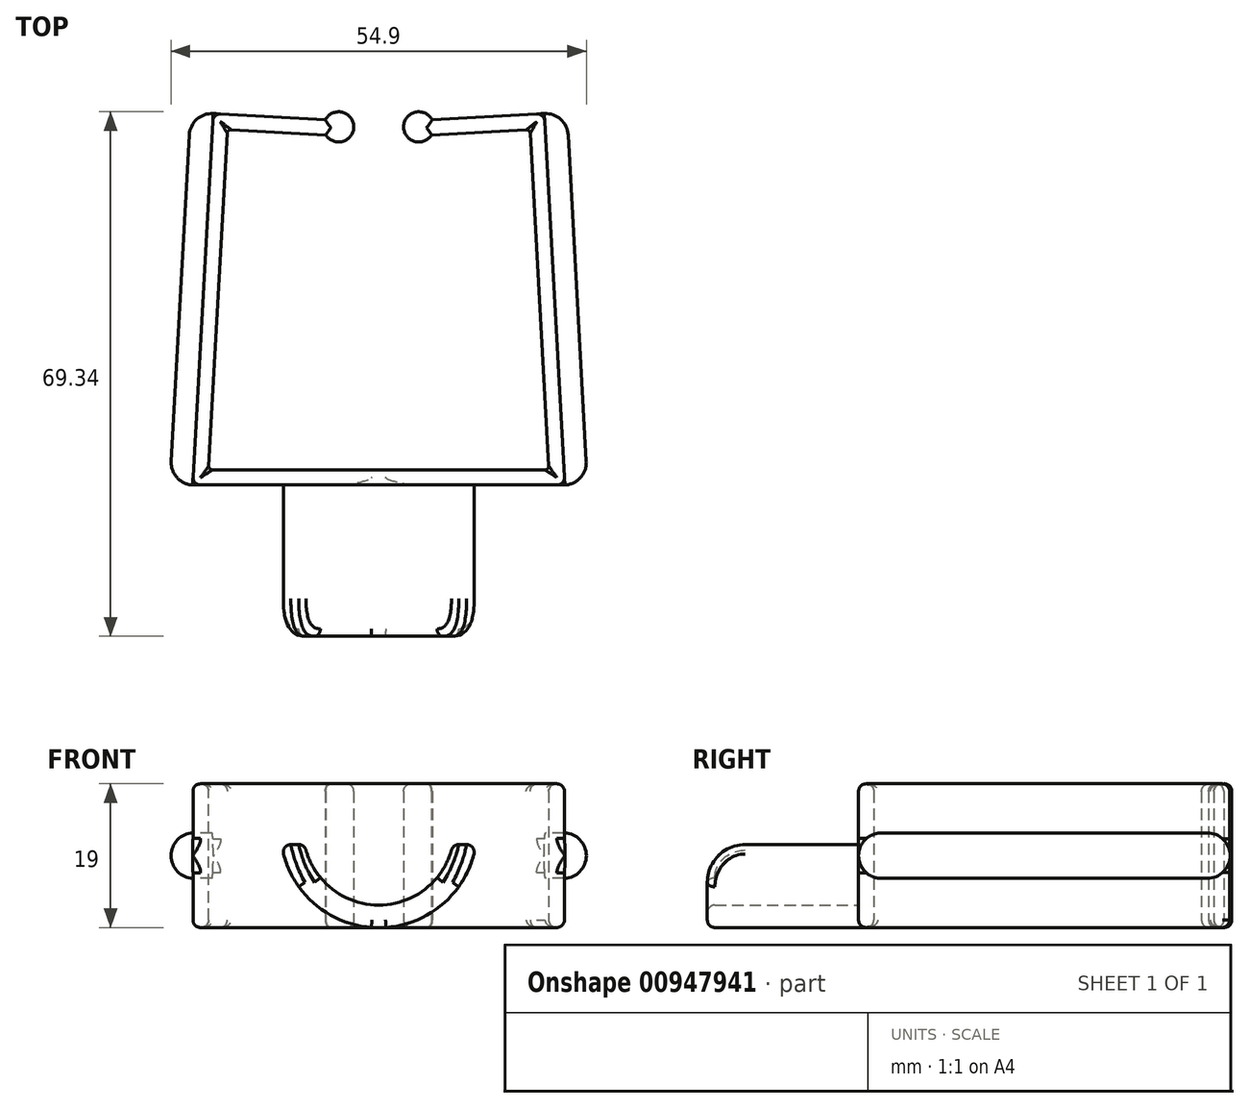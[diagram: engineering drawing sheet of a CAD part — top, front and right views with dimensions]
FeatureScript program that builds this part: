
annotation { "Feature Type Name" : "Feature", "Feature Type Description" : "" }
export const myFeature = defineFeature(function(context is Context, id is Id, definition is map)
    precondition{}
    {
        {
            var Q0;
            Q0=qCreatedBy(makeId("Top.planeOp"),FACE);
            var sketch = newSketch(context, id + "F0", { "sketchPlane" : qUnion([Q0])});
            skLineSegment(sketch, "E0", {"start": v(0, -31.5) * mm, "end": v(22.5, -31.5) * mm});
            skLineSegment(sketch, "E1", {"start": v(20, 13.5) * mm, "end": v(22.5, -31.5) * mm});
            skLineSegment(sketch, "E2", {"start": v(20, 13.5) * mm, "end": v(7, 12.78) * mm});
            skLineSegment(sketch, "E3.0", {"start": v(0, -33.5) * mm, "end": v(24.62, -33.5) * mm});
            skLineSegment(sketch, "E4.0", {"start": v(21.89, 15.61) * mm, "end": v(24.62, -33.5) * mm});
            skLineSegment(sketch, "E5.0", {"start": v(21.89, 15.61) * mm, "end": v(7.06, 14.8) * mm});
            skLineSegment(sketch, "E6.MirrorCS", {"start": v(-21.88, 15.61) * mm, "end": v(-24.61, -33.5) * mm});
            skLineSegment(sketch, "E7.MirrorCS", {"start": v(-20, 13.5) * mm, "end": v(-22.5, -31.5) * mm});
            skLineSegment(sketch, "E8.MirrorCS", {"start": v(0, -31.5) * mm, "end": v(-22.5, -31.5) * mm});
            skLineSegment(sketch, "E9.MirrorCS", {"start": v(0, -33.5) * mm, "end": v(-24.61, -33.5) * mm});
            skArc(sketch, "E10", {"start": v(7.06, 14.8) * mm, "mid": v(3.3, 13.92) * mm, "end": v(7, 12.78) * mm});
            skLineSegment(sketch, "E11.MirrorCS", {"start": v(-21.89, 15.61) * mm, "end": v(-7.06, 14.8) * mm});
            skLineSegment(sketch, "E12.MirrorCS", {"start": v(-20, 13.5) * mm, "end": v(-7, 12.78) * mm});
            skArc(sketch, "E13.MirrorCS", {"start": v(-7.06, 14.8) * mm, "mid": v(-3.3, 13.92) * mm, "end": v(-7, 12.78) * mm});
            skSolve(sketch);
        }
        {
            var Q0;
            Q0=makeQuery(id+"F0.imprint","IMPRINT",FACE,{"disambiguationData":[TD([[makeQuery(id+"F0.imprint","IMPRINT",EDGE,{"derivedFrom":sQuery(id+"F0.wireOp",EDGE,"E0")}),-1.0]])]});
            extrude(context, id + "F1", {"entities" : qUnion([Q0]), "depth" : 19 * mm, "offsetDistance" : 25 * mm});
        }
        {
            var Q0;
            Q0=makeQuery(id+"F1.opExtrude","SWEPT_FACE",FACE,{"disambiguationData":[OSD([sQuery(id+"F0.wireOp",EDGE,"E6.MirrorCS")])]});
            var sketch = newSketch(context, id + "F2", { "sketchPlane" : qUnion([Q0])});
            skLineSegment(sketch, "E14", {"start": v(-14.38, 12.5) * mm, "end": v(34.8, 12.5) * mm});
            skLineSegment(sketch, "E15", {"start": v(-14.38, 6.5) * mm, "end": v(34.8, 6.5) * mm});
            skLineSegment(sketch, "E16", {"start": v(-14.38, 12.5) * mm, "end": v(-14.38, 6.5) * mm});
            skLineSegment(sketch, "E17", {"start": v(34.8, 12.5) * mm, "end": v(34.8, 6.5) * mm});
            skSolve(sketch);
        }
        {
            var Q0;
            Q0=makeQuery(id+"F2.imprint","IMPRINT",FACE,{"disambiguationData":[TD([[makeQuery(id+"F2.imprint","IMPRINT",EDGE,{"derivedFrom":sQuery(id+"F2.wireOp",EDGE,"E14")}),-1.0]])]});
            extrude(context, id + "F3", {"entities" : qUnion([Q0]), "operationType" : NewBodyOperationType.ADD, "depth" : 3 * mm, "offsetDistance" : 25 * mm});
        }
        {
            var Q0;
            Q0=makeQuery(id+"F1.opExtrude","SWEPT_FACE",FACE,{"disambiguationData":[OSD([sQuery(id+"F0.wireOp",EDGE,"E4.0")])]});
            var sketch = newSketch(context, id + "F4", { "sketchPlane" : qUnion([Q0])});
            skLineSegment(sketch, "E18", {"start": v(-34.8, 12.5) * mm, "end": v(14.38, 12.5) * mm});
            skLineSegment(sketch, "E19", {"start": v(-34.8, 6.5) * mm, "end": v(14.38, 6.5) * mm});
            skLineSegment(sketch, "E20", {"start": v(-34.8, 12.5) * mm, "end": v(-34.8, 6.5) * mm});
            skLineSegment(sketch, "E21", {"start": v(14.38, 12.5) * mm, "end": v(14.38, 6.5) * mm});
            skSolve(sketch);
        }
        {
            var Q0;
            Q0=makeQuery(id+"F4.imprint","IMPRINT",FACE,{"disambiguationData":[TD([[makeQuery(id+"F4.imprint","IMPRINT",EDGE,{"derivedFrom":sQuery(id+"F4.wireOp",EDGE,"E18")}),-1.0]])]});
            extrude(context, id + "F5", {"entities" : qUnion([Q0]), "operationType" : NewBodyOperationType.ADD, "depth" : 3 * mm, "offsetDistance" : 25 * mm});
        }
        {
            var Q0;
            Q0=makeQuery(id+"F5.opExtrude","CAP_EDGE",EDGE,{"disambiguationData":[OSD([sQuery(id+"F4.wireOp",EDGE,"E18")])],"isStart":false});
            var Q1;
            Q1=makeQuery(id+"F5.opExtrude","CAP_EDGE",EDGE,{"disambiguationData":[OSD([sQuery(id+"F4.wireOp",EDGE,"E19")])],"isStart":false});
            var Q2;
            Q2=makeQuery(id+"F5.opExtrude","CAP_EDGE",EDGE,{"disambiguationData":[OSD([sQuery(id+"F4.wireOp",EDGE,"E20")])],"isStart":false});
            var Q3;
            Q3=makeQuery(id+"F5.opExtrude","SWEPT_EDGE",EDGE,{"disambiguationData":[OSD([sQuery(id+"F0.wireOp",EDGE,"E3.0"),sQuery(id+"F0.wireOp",EDGE,"E4.0"),sQuery(id+"F4.wireOp",EDGE,"E18"),sQuery(id+"F4.wireOp",EDGE,"E20")])]});
            var Q4;
            Q4=makeQuery(id+"F5.opExtrude","SWEPT_EDGE",EDGE,{"disambiguationData":[OSD([sQuery(id+"F0.wireOp",EDGE,"E3.0"),sQuery(id+"F0.wireOp",EDGE,"E4.0"),sQuery(id+"F4.wireOp",EDGE,"E19"),sQuery(id+"F4.wireOp",EDGE,"E20")])]});
            var Q5;
            Q5=makeQuery(id+"F5.opExtrude","CAP_EDGE",EDGE,{"disambiguationData":[OSD([sQuery(id+"F4.wireOp",EDGE,"E21")])],"isStart":false});
            var Q6;
            Q6=makeQuery(id+"F5.opExtrude","SWEPT_EDGE",EDGE,{"disambiguationData":[OSD([sQuery(id+"F0.wireOp",EDGE,"E4.0"),sQuery(id+"F0.wireOp",EDGE,"E5.0"),sQuery(id+"F4.wireOp",EDGE,"E18"),sQuery(id+"F4.wireOp",EDGE,"E21")])]});
            var Q7;
            Q7=makeQuery(id+"F5.opExtrude","SWEPT_EDGE",EDGE,{"disambiguationData":[OSD([sQuery(id+"F0.wireOp",EDGE,"E4.0"),sQuery(id+"F0.wireOp",EDGE,"E5.0"),sQuery(id+"F4.wireOp",EDGE,"E19"),sQuery(id+"F4.wireOp",EDGE,"E21")])]});
            var Q8;
            Q8=makeQuery(id+"F3.opExtrude","CAP_EDGE",EDGE,{"disambiguationData":[OSD([sQuery(id+"F2.wireOp",EDGE,"E14")])],"isStart":false});
            var Q9;
            Q9=makeQuery(id+"F3.opExtrude","CAP_EDGE",EDGE,{"disambiguationData":[OSD([sQuery(id+"F2.wireOp",EDGE,"E15")])],"isStart":false});
            var Q10;
            Q10=makeQuery(id+"F3.opExtrude","CAP_EDGE",EDGE,{"disambiguationData":[OSD([sQuery(id+"F2.wireOp",EDGE,"E16")])],"isStart":false});
            var Q11;
            Q11=makeQuery(id+"F3.opExtrude","SWEPT_EDGE",EDGE,{"disambiguationData":[OSD([sQuery(id+"F0.wireOp",EDGE,"571edef0-3b51-43ca-9341-9ceadd8f7e81.MirrorCS"),sQuery(id+"F0.wireOp",EDGE,"E6.MirrorCS"),sQuery(id+"F2.wireOp",EDGE,"E15"),sQuery(id+"F2.wireOp",EDGE,"E16")])]});
            var Q12;
            Q12=makeQuery(id+"F3.opExtrude","SWEPT_EDGE",EDGE,{"disambiguationData":[OSD([sQuery(id+"F0.wireOp",EDGE,"571edef0-3b51-43ca-9341-9ceadd8f7e81.MirrorCS"),sQuery(id+"F0.wireOp",EDGE,"E6.MirrorCS"),sQuery(id+"F2.wireOp",EDGE,"E14"),sQuery(id+"F2.wireOp",EDGE,"E16")])]});
            var Q13;
            Q13=makeQuery(id+"F3.opExtrude","CAP_EDGE",EDGE,{"disambiguationData":[OSD([sQuery(id+"F2.wireOp",EDGE,"E17")])],"isStart":false});
            var Q14;
            Q14=makeQuery(id+"F3.opExtrude","SWEPT_EDGE",EDGE,{"disambiguationData":[OSD([sQuery(id+"F0.wireOp",EDGE,"E6.MirrorCS"),sQuery(id+"F0.wireOp",EDGE,"E9.MirrorCS"),sQuery(id+"F2.wireOp",EDGE,"E14"),sQuery(id+"F2.wireOp",EDGE,"E17")])]});
            var Q15;
            Q15=makeQuery(id+"F3.opExtrude","SWEPT_EDGE",EDGE,{"disambiguationData":[OSD([sQuery(id+"F0.wireOp",EDGE,"E6.MirrorCS"),sQuery(id+"F0.wireOp",EDGE,"E9.MirrorCS"),sQuery(id+"F2.wireOp",EDGE,"E15"),sQuery(id+"F2.wireOp",EDGE,"E17")])]});
            fillet(context, id + "F6", {"entities" : qUnion([Q0, Q1, Q2, Q3, Q4, Q5, Q6, Q7, Q8, Q9, Q10, Q11, Q12, Q13, Q14, Q15]), "radius" : 3 * mm, "tangentPropagation" : true, "allowEdgeOverflow" : false});
        }
        {
            var Q0;
            Q0=makeQuery(id+"F1.opExtrude","SWEPT_FACE",FACE,{"disambiguationData":[OSD([sQuery(id+"F0.wireOp",EDGE,"E3.0"),sQuery(id+"F0.wireOp",EDGE,"E9.MirrorCS")])]});
            var sketch = newSketch(context, id + "F7", { "sketchPlane" : qUnion([Q0])});
            skArc(sketch, "E22", {"start": v(-9.8, 10.97) * mm, "mid": v(0, 2.97) * mm, "end": v(9.8, 10.97) * mm});
            skLineSegment(sketch, "E23", {"start": v(-9.8, 10.97) * mm, "end": v(-12.82, 10.97) * mm});
            skLineSegment(sketch, "E24", {"start": v(9.8, 10.97) * mm, "end": v(12.85, 10.97) * mm});
            skArc(sketch, "E25", {"start": v(-12.85, 10.97) * mm, "mid": v(0, -0.03) * mm, "end": v(12.85, 10.97) * mm});
            skLineSegment(sketch, "E26", {"start": v(-12.82, 10.97) * mm, "end": v(-12.85, 10.97) * mm});
            skPoint(sketch, "E27.start.orphan", {"position": v(0, 0) * mm});
            skSolve(sketch);
        }
        {
            var Q0;
            Q0=makeQuery(id+"F7.imprint","IMPRINT",FACE,{"disambiguationData":[TD([[makeQuery(id+"F7.imprint","IMPRINT",EDGE,{"derivedFrom":sQuery(id+"F7.wireOp",EDGE,"E22")}),-1.0]])]});
            extrude(context, id + "F8", {"entities" : qUnion([Q0]), "operationType" : NewBodyOperationType.ADD, "depth" : 20 * mm, "offsetDistance" : 25 * mm});
        }
        {
            var Q0;
            Q0=makeQuery(id+"F8.opExtrude","CAP_EDGE",EDGE,{"disambiguationData":[OSD([sQuery(id+"F7.wireOp",EDGE,"E27"),sQuery(id+"F7.wireOp",EDGE,"a4f32ab0-1648-429d-a977-f9504d9d67a10.MirrorCS")])],"isStart":false});
            var Q1;
            Q1=makeQuery(id+"F8.opExtrude","SWEPT_EDGE",EDGE,{"disambiguationData":[OSD([sQuery(id+"F7.wireOp",EDGE,"a4f32ab0-1648-429d-a977-f9504d9d67a10.MirrorCS"),sQuery(id+"F7.wireOp",EDGE,"80b11956-c133-4d79-b513-8fb03a3275040.MirrorCS")])]});
            var Q2;
            Q2=makeQuery(id+"F8.opExtrude","SWEPT_EDGE",EDGE,{"disambiguationData":[OSD([sQuery(id+"F7.wireOp",EDGE,"EQUY75fL-QU1j-GgtN-3R5t-ZK2hIXwrbhZ0"),sQuery(id+"F7.wireOp",EDGE,"E27")])]});
            var Q3;
            {var subQ0=sQuery(id+"F7.wireOp",EDGE,"E25");Q3=makeQuery(id+"F8.opExtrude","CAP_EDGE",EDGE,{"disambiguationData":[OSD([subQ0]),TDD([makeQuery(id+"F7.imprint","IMPRINT",EDGE,{"disambiguationData":[TD([[makeQuery(id+"F7.imprint","INTERSECT",VERTEX,{"derivedFrom":[subQ0,sQuery(id+"F7.wireOp",EDGE,"E26")]}),-1.0]])],"derivedFrom":subQ0})])],"isStart":false});}
            var Q4;
            Q4=makeQuery(id+"F8.opExtrude","CAP_EDGE",EDGE,{"disambiguationData":[OSD([sQuery(id+"F7.wireOp",EDGE,"E22")])],"isStart":false});
            var Q5;
            Q5=makeQuery(id+"F8.opExtrude","SWEPT_EDGE",EDGE,{"disambiguationData":[OSD([sQuery(id+"F7.wireOp",EDGE,"E25"),sQuery(id+"F7.wireOp",EDGE,"E26")])]});
            var Q6;
            Q6=makeQuery(id+"F8.opExtrude","SWEPT_EDGE",EDGE,{"disambiguationData":[OSD([sQuery(id+"F7.wireOp",EDGE,"E22"),sQuery(id+"F7.wireOp",EDGE,"E24")])]});
            var Q7;
            Q7=makeQuery(id+"F8.opExtrude","SWEPT_EDGE",EDGE,{"disambiguationData":[OSD([sQuery(id+"F7.wireOp",EDGE,"E24"),sQuery(id+"F7.wireOp",EDGE,"E25")])]});
            var Q8;
            Q8=makeQuery(id+"F8.opExtrude","SWEPT_EDGE",EDGE,{"disambiguationData":[OSD([sQuery(id+"F7.wireOp",EDGE,"E22"),sQuery(id+"F7.wireOp",EDGE,"E23")])]});
            fillet(context, id + "F9", {"entities" : qUnion([Q0, Q1, Q2, Q3, Q4, Q5, Q6, Q7, Q8]), "radius" : 1 * mm, "tangentPropagation" : true, "allowEdgeOverflow" : false});
        }
        {
            var Q0;
            Q0=makeQuery(id+"F8.opExtrude","CAP_EDGE",EDGE,{"disambiguationData":[OSD([sQuery(id+"F7.wireOp",EDGE,"EQUY75fL-QU1j-GgtN-3R5t-ZK2hIXwrbhZ0")])],"isStart":false});
            var Q1;
            Q1=makeQuery(id+"F8.opExtrude","CAP_EDGE",EDGE,{"disambiguationData":[OSD([sQuery(id+"F7.wireOp",EDGE,"80b11956-c133-4d79-b513-8fb03a3275040.MirrorCS")])],"isStart":false});
            var Q2;
            Q2=makeQuery(id+"F8.opExtrude","CAP_EDGE",EDGE,{"disambiguationData":[OSD([sQuery(id+"F7.wireOp",EDGE,"E23"),sQuery(id+"F7.wireOp",EDGE,"E26")])],"isStart":false});
            var Q3;
            Q3=makeQuery(id+"F8.opExtrude","CAP_EDGE",EDGE,{"disambiguationData":[OSD([sQuery(id+"F7.wireOp",EDGE,"E24")])],"isStart":false});
            fillet(context, id + "F10", {"entities" : qUnion([Q0, Q1, Q2, Q3]), "radius" : 5 * mm, "tangentPropagation" : true, "allowEdgeOverflow" : false});
        }
        {
            var Q0;
            Q0=makeQuery(id+"F1.opExtrude","CAP_EDGE",EDGE,{"disambiguationData":[OSD([sQuery(id+"F0.wireOp",EDGE,"E3.0"),sQuery(id+"F0.wireOp",EDGE,"E9.MirrorCS"),sQuery(id+"F0.wireOp",EDGE,"hYxik0ZY-ueu8-ayZR-DYAp-35rbcAyUoamW")])],"isStart":false});
            var Q1;
            Q1=makeQuery(id+"F1.opExtrude","CAP_EDGE",EDGE,{"disambiguationData":[OSD([sQuery(id+"F0.wireOp",EDGE,"E0"),sQuery(id+"F0.wireOp",EDGE,"E8.MirrorCS"),sQuery(id+"F0.wireOp",EDGE,"1KXFA9ki-KhNV-2GeL-JZVf-4Y6hzvoB7xsB")])],"isStart":false});
            var Q2;
            Q2=makeQuery(id+"F1.opExtrude","SWEPT_EDGE",EDGE,{"disambiguationData":[OSD([sQuery(id+"F0.wireOp",EDGE,"E3.0"),sQuery(id+"F0.wireOp",EDGE,"E4.0")])]});
            var Q3;
            {var subQ1=sQuery(id+"F0.wireOp",EDGE,"hYxik0ZY-ueu8-ayZR-DYAp-35rbcAyUoamW");var subQ2=sQuery(id+"F0.wireOp",EDGE,"E9.MirrorCS");var subQ3=sQuery(id+"F0.wireOp",EDGE,"E3.0");var subQ4=makeQuery(id+"F1.opExtrude","CAP_EDGE",EDGE,{"disambiguationData":[OSD([subQ3,subQ2,subQ1])],"isStart":true});var subQ5=sQuery(id+"F0.wireOp",EDGE,"E4.0");Q3=makeQuery(id+"F8.boolean.opBoolean","SPLIT",EDGE,{"disambiguationData":[TD([makeQuery(id+"F1.opExtrude","SWEPT_FACE",FACE,{"disambiguationData":[OSD([subQ5])]})])],"derivedFrom":subQ4});}
            var Q4;
            {var subQ1=sQuery(id+"F0.wireOp",EDGE,"hYxik0ZY-ueu8-ayZR-DYAp-35rbcAyUoamW");var subQ2=sQuery(id+"F0.wireOp",EDGE,"E9.MirrorCS");var subQ3=sQuery(id+"F0.wireOp",EDGE,"E3.0");var subQ4=makeQuery(id+"F1.opExtrude","CAP_EDGE",EDGE,{"disambiguationData":[OSD([subQ3,subQ2,subQ1])],"isStart":true});var subQ5=sQuery(id+"F0.wireOp",EDGE,"E6.MirrorCS");Q4=makeQuery(id+"F8.boolean.opBoolean","SPLIT",EDGE,{"disambiguationData":[TD([makeQuery(id+"F1.opExtrude","SWEPT_FACE",FACE,{"disambiguationData":[OSD([subQ5])]})])],"derivedFrom":subQ4});}
            var Q5;
            Q5=makeQuery(id+"F1.opExtrude","SWEPT_EDGE",EDGE,{"disambiguationData":[OSD([sQuery(id+"F0.wireOp",EDGE,"E6.MirrorCS"),sQuery(id+"F0.wireOp",EDGE,"E9.MirrorCS")])]});
            var Q6;
            Q6=makeQuery(id+"F1.opExtrude","CAP_EDGE",EDGE,{"disambiguationData":[OSD([sQuery(id+"F0.wireOp",EDGE,"E4.0")])],"isStart":false});
            var Q7;
            Q7=makeQuery(id+"F1.opExtrude","CAP_EDGE",EDGE,{"disambiguationData":[OSD([sQuery(id+"F0.wireOp",EDGE,"E1")])],"isStart":false});
            var Q8;
            Q8=makeQuery(id+"F1.opExtrude","CAP_EDGE",EDGE,{"disambiguationData":[OSD([sQuery(id+"F0.wireOp",EDGE,"E2")])],"isStart":false});
            var Q9;
            Q9=makeQuery(id+"F1.opExtrude","CAP_EDGE",EDGE,{"disambiguationData":[OSD([sQuery(id+"F0.wireOp",EDGE,"E5.0")])],"isStart":false});
            var Q10;
            Q10=makeQuery(id+"F1.opExtrude","CAP_EDGE",EDGE,{"disambiguationData":[OSD([sQuery(id+"F0.wireOp",EDGE,"E10")])],"isStart":false});
            var Q11;
            Q11=makeQuery(id+"F1.opExtrude","CAP_EDGE",EDGE,{"disambiguationData":[OSD([sQuery(id+"F0.wireOp",EDGE,"E10")])],"isStart":true});
            var Q12;
            Q12=makeQuery(id+"F1.opExtrude","CAP_EDGE",EDGE,{"disambiguationData":[OSD([sQuery(id+"F0.wireOp",EDGE,"E2")])],"isStart":true});
            var Q13;
            Q13=makeQuery(id+"F1.opExtrude","CAP_EDGE",EDGE,{"disambiguationData":[OSD([sQuery(id+"F0.wireOp",EDGE,"E0"),sQuery(id+"F0.wireOp",EDGE,"E8.MirrorCS"),sQuery(id+"F0.wireOp",EDGE,"1KXFA9ki-KhNV-2GeL-JZVf-4Y6hzvoB7xsB")])],"isStart":true});
            var Q14;
            {var subQ0=sQuery(id+"F0.wireOp",EDGE,"hYxik0ZY-ueu8-ayZR-DYAp-35rbcAyUoamW");var subQ1=sQuery(id+"F0.wireOp",EDGE,"E9.MirrorCS");var subQ2=sQuery(id+"F0.wireOp",EDGE,"E3.0");Q14=makeQuery(id+"F8.boolean.opBoolean","MERGE",FACE,{"derivedFrom":[makeQuery(id+"F1.opExtrude","CAP_FACE",FACE,{"disambiguationData":[OSD([sQuery(id+"F0.wireOp",EDGE,"E0"),sQuery(id+"F0.wireOp",EDGE,"E1"),sQuery(id+"F0.wireOp",EDGE,"E2"),subQ2,sQuery(id+"F0.wireOp",EDGE,"E4.0"),sQuery(id+"F0.wireOp",EDGE,"E5.0"),sQuery(id+"F0.wireOp",EDGE,"571edef0-3b51-43ca-9341-9ceadd8f7e81.MirrorCS"),sQuery(id+"F0.wireOp",EDGE,"ae7ddd86-a618-4762-a295-861e5166ab92.MirrorCS"),sQuery(id+"F0.wireOp",EDGE,"E6.MirrorCS"),sQuery(id+"F0.wireOp",EDGE,"E7.MirrorCS"),sQuery(id+"F0.wireOp",EDGE,"E8.MirrorCS"),subQ1,sQuery(id+"F0.wireOp",EDGE,"E10"),sQuery(id+"F0.wireOp",EDGE,"08d02471-9061-488d-b145-d664c3251d19.MirrorC"),sQuery(id+"F0.wireOp",EDGE,"1KXFA9ki-KhNV-2GeL-JZVf-4Y6hzvoB7xsB"),subQ0])],"isStart":true}),makeQuery(id+"F8.opExtrude","SWEPT_FACE",FACE,{"disambiguationData":[OSD([subQ2,subQ1,subQ0])]})]});}
            var Q15;
            Q15=makeQuery(id+"F1.opExtrude","CAP_EDGE",EDGE,{"disambiguationData":[OSD([sQuery(id+"F0.wireOp",EDGE,"571edef0-3b51-43ca-9341-9ceadd8f7e81.MirrorCS")])],"isStart":false});
            var Q16;
            Q16=makeQuery(id+"F1.opExtrude","CAP_EDGE",EDGE,{"disambiguationData":[OSD([sQuery(id+"F0.wireOp",EDGE,"08d02471-9061-488d-b145-d664c3251d19.MirrorC")])],"isStart":false});
            var Q17;
            Q17=makeQuery(id+"F1.opExtrude","CAP_EDGE",EDGE,{"disambiguationData":[OSD([sQuery(id+"F0.wireOp",EDGE,"E6.MirrorCS")])],"isStart":false});
            var Q18;
            Q18=makeQuery(id+"F1.opExtrude","CAP_EDGE",EDGE,{"disambiguationData":[OSD([sQuery(id+"F0.wireOp",EDGE,"E7.MirrorCS")])],"isStart":false});
            var Q19;
            {var subQ0=sQuery(id+"F0.wireOp",EDGE,"E5.0");var subQ1=makeQuery(id+"F1.opExtrude","SWEPT_FACE",FACE,{"disambiguationData":[OSD([subQ0])]});var subQ2=sQuery(id+"F4.wireOp",EDGE,"E19");var subQ3=makeQuery(id+"F5.opExtrude","CAP_FACE",FACE,{"disambiguationData":[OSD([sQuery(id+"F4.wireOp",EDGE,"E18"),subQ2,sQuery(id+"F4.wireOp",EDGE,"E20"),sQuery(id+"F4.wireOp",EDGE,"E21")])],"isStart":true});var subQ4=sQuery(id+"F0.wireOp",EDGE,"E4.0");var subQ5=makeQuery(id+"F1.opExtrude","SWEPT_EDGE",EDGE,{"disambiguationData":[OSD([subQ4,subQ0])]});var subQ6=makeQuery(id+"F1.opExtrude","SWEPT_FACE",FACE,{"disambiguationData":[OSD([subQ4])]});Q19=makeQuery(id+"F6.opFillet","MERGE",EDGE,{"derivedFrom":[makeQuery(id+"F5.boolean.opBoolean","SPLIT",EDGE,{"disambiguationData":[topologyDisambiguationEdgeConnected([subQ6,subQ1]),TD([makeQuery(id+"F5.opExtrude","SWEPT_FACE",FACE,{"disambiguationData":[OSD([subQ2])]})])],"derivedFrom":subQ5}),makeQuery(id+"F5.boolean.opBoolean","SPLIT",EDGE,{"disambiguationData":[topologyDisambiguationEdgeConnected([subQ1,subQ3])],"derivedFrom":subQ5})]});}
            var Q20;
            {var subQ0=sQuery(id+"F0.wireOp",EDGE,"571edef0-3b51-43ca-9341-9ceadd8f7e81.MirrorCS");var subQ1=makeQuery(id+"F1.opExtrude","SWEPT_FACE",FACE,{"disambiguationData":[OSD([subQ0])]});var subQ2=sQuery(id+"F2.wireOp",EDGE,"E14");var subQ3=makeQuery(id+"F3.opExtrude","CAP_FACE",FACE,{"disambiguationData":[OSD([subQ2,sQuery(id+"F2.wireOp",EDGE,"E15"),sQuery(id+"F2.wireOp",EDGE,"E16"),sQuery(id+"F2.wireOp",EDGE,"E17")])],"isStart":true});var subQ4=sQuery(id+"F0.wireOp",EDGE,"E6.MirrorCS");var subQ5=makeQuery(id+"F1.opExtrude","SWEPT_EDGE",EDGE,{"disambiguationData":[OSD([subQ0,subQ4])]});var subQ6=makeQuery(id+"F1.opExtrude","SWEPT_FACE",FACE,{"disambiguationData":[OSD([subQ4])]});Q20=makeQuery(id+"F6.opFillet","MERGE",EDGE,{"derivedFrom":[makeQuery(id+"F3.boolean.opBoolean","SPLIT",EDGE,{"disambiguationData":[topologyDisambiguationEdgeConnected([subQ1,subQ6]),TD([makeQuery(id+"F3.opExtrude","SWEPT_FACE",FACE,{"disambiguationData":[OSD([subQ2])]})])],"derivedFrom":subQ5}),makeQuery(id+"F3.boolean.opBoolean","SPLIT",EDGE,{"disambiguationData":[topologyDisambiguationEdgeConnected([subQ1,subQ3])],"derivedFrom":subQ5})]});}
            var Q21;
            Q21=makeQuery(id+"F8.opExtrude","CAP_EDGE",EDGE,{"disambiguationData":[OSD([sQuery(id+"F7.wireOp",EDGE,"E22")])],"isStart":true});
            var Q22;
            Q22=makeQuery(id+"F1.opExtrude","CAP_EDGE",EDGE,{"disambiguationData":[OSD([sQuery(id+"F0.wireOp",EDGE,"ae7ddd86-a618-4762-a295-861e5166ab92.MirrorCS")])],"isStart":false});
            var Q23;
            Q23=makeQuery(id+"F1.opExtrude","CAP_EDGE",EDGE,{"disambiguationData":[OSD([sQuery(id+"F0.wireOp",EDGE,"E11.MirrorCS")])],"isStart":false});
            var Q24;
            Q24=makeQuery(id+"F1.opExtrude","CAP_EDGE",EDGE,{"disambiguationData":[OSD([sQuery(id+"F0.wireOp",EDGE,"E12.MirrorCS")])],"isStart":false});
            var Q25;
            Q25=makeQuery(id+"F1.opExtrude","CAP_EDGE",EDGE,{"disambiguationData":[OSD([sQuery(id+"F0.wireOp",EDGE,"E13.MirrorCS")])],"isStart":false});
            var Q26;
            {var subQ0=sQuery(id+"F0.wireOp",EDGE,"E4.0");var subQ1=sQuery(id+"F0.wireOp",EDGE,"E5.0");Q26=makeQuery(id+"F5.boolean.opBoolean","SPLIT",EDGE,{"disambiguationData":[TD([makeQuery(id+"F5.opExtrude","SWEPT_FACE",FACE,{"disambiguationData":[OSD([sQuery(id+"F4.wireOp",EDGE,"E18")])]})])],"derivedFrom":makeQuery(id+"F1.opExtrude","SWEPT_EDGE",EDGE,{"disambiguationData":[OSD([subQ0,subQ1])]})});}
            var Q27;
            {var subQ0=sQuery(id+"F0.wireOp",EDGE,"E11.MirrorCS");var subQ1=sQuery(id+"F0.wireOp",EDGE,"E6.MirrorCS");Q27=makeQuery(id+"F3.boolean.opBoolean","SPLIT",EDGE,{"disambiguationData":[TD([makeQuery(id+"F3.opExtrude","SWEPT_FACE",FACE,{"disambiguationData":[OSD([sQuery(id+"F2.wireOp",EDGE,"E14")])]})])],"derivedFrom":makeQuery(id+"F1.opExtrude","SWEPT_EDGE",EDGE,{"disambiguationData":[OSD([subQ1,subQ0])]})});}
            fillet(context, id + "F11", {"entities" : qUnion([Q0, Q1, Q2, Q3, Q4, Q5, Q6, Q7, Q8, Q9, Q10, Q11, Q12, Q13, Q14, Q15, Q16, Q17, Q18, Q19, Q20, Q21, Q22, Q23, Q24, Q25, Q26, Q27]), "radius" : 1 * mm, "tangentPropagation" : true, "allowEdgeOverflow" : false});
        }
        {
            var Q0;
            Q0=makeQuery(id+"F1.opExtrude","SWEPT_FACE",FACE,{"disambiguationData":[OSD([sQuery(id+"F0.wireOp",EDGE,"E1")])]});
            var Q1;
            Q1=makeQuery(id+"F1.opExtrude","SWEPT_FACE",FACE,{"disambiguationData":[OSD([sQuery(id+"F0.wireOp",EDGE,"E0"),sQuery(id+"F0.wireOp",EDGE,"E8.MirrorCS")])]});
            var Q2;
            Q2=makeQuery(id+"F1.opExtrude","SWEPT_FACE",FACE,{"disambiguationData":[OSD([sQuery(id+"F0.wireOp",EDGE,"E7.MirrorCS")])]});
            fillet(context, id + "F12", {"entities" : qUnion([Q0, Q1, Q2]), "radius" : .5 * mm, "tangentPropagation" : true, "allowEdgeOverflow" : false});
        }
    });
